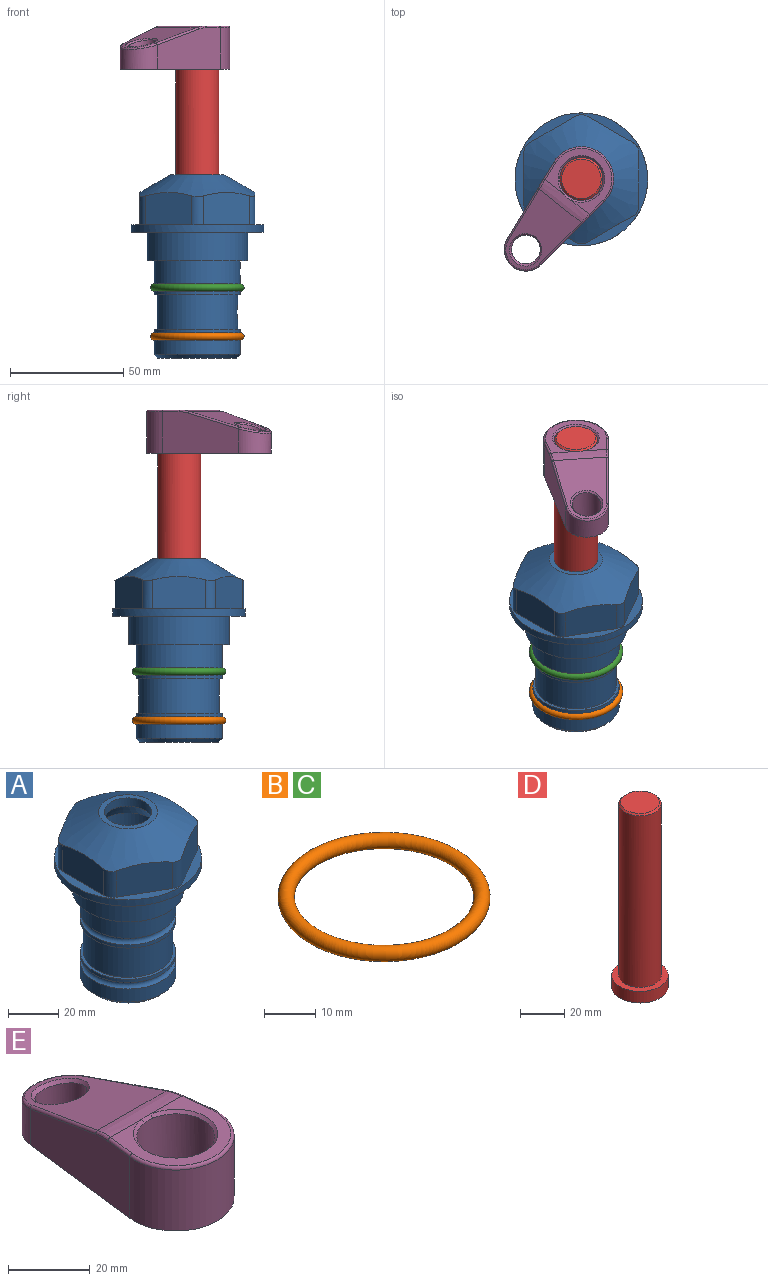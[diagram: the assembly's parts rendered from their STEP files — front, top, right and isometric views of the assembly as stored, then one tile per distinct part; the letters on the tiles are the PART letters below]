
ASSEMBLY  parts=5 mates=3
PART A: 36 faces, bbox 58.7x58.7x81 mm
  f0: cylinder r=17.78mm len=35.56mm, axis (0,0,1), area 1670.8mm2, adj f23,f24,f31
  f1: cylinder r=19.05mm len=38.1mm, axis (0,0,1), area 1191.9mm2, adj f26,f27,f30
  f2: plane 58.66x58.66mm, normal (0,0,-1), area 1150.6mm2, adj f3,f28
  f3: cylinder r=29.33mm len=58.66mm, axis (0,0,-1), area 585.1mm2, adj f2,f4
  f4: plane 58.66x58.66mm, normal (0,0,1), area 475.9mm2, adj f3,f5,f6,f7,f8,f9,f10,f11
  f5: plane 20.32x14.34mm, normal (-0.5,0.87,0), area 324.4mm2, adj f4,f15,f16,f17
  f6: plane 20.32x14.34mm, normal (0.5,0.87,0), area 324.4mm2, adj f4,f14,f15,f17
  f7: plane 23.48x14.34mm, normal (1,0,0), area 324.4mm2, adj f4,f13,f14,f17
  f8: plane 20.32x14.34mm, normal (0.5,-0.87,0), area 324.4mm2, adj f4,f12,f13,f17
  f9: plane 20.32x14.34mm, normal (-0.5,-0.87,0), area 324.4mm2, adj f4,f11,f12,f17
  f10: plane 23.48x14.34mm, normal (-1,0,0), area 324.4mm2, adj f4,f11,f16,f17
  f11: cylinder r=5.08mm len=12.85mm, axis (0,0,-1), area 67.2mm2, adj f4,f9,f10,f17
  f12: cylinder r=5.08mm len=12.85mm, axis (0,0,-1), area 67.2mm2, adj f4,f8,f9,f17
  f13: cylinder r=5.08mm len=12.85mm, axis (0,0,-1), area 67.2mm2, adj f4,f7,f8,f17
  f14: cylinder r=5.08mm len=12.85mm, axis (0,0,-1), area 67.2mm2, adj f4,f6,f7,f17
  f15: cylinder r=5.08mm len=12.85mm, axis (0,0,-1), area 67.2mm2, adj f4,f5,f6,f17
  f16: cylinder r=5.08mm len=12.85mm, axis (0,0,-1), area 67.2mm2, adj f4,f5,f10,f17
  f17: cone r=11.73mm half-angle=60deg, axis (0,0,-1), area 2071.8mm2, adj f5,f6,f7,f8,f9,f10,f11,f12
  f18: plane 23.46x23.46mm, normal (0,0,1), area 147.4mm2, adj f17,f35
  f19: plane 34.93x34.93mm, normal (0,0,-1), area 958mm2, adj f29
  f20: cylinder r=19.05mm len=38.1mm, axis (0,0,1), area 760.1mm2, adj f21,f29
  f21: torus R=19.05mm, axis (0,0,1), area 565.3mm2, adj f20,f22
  f22: cylinder r=19.05mm len=38.1mm, axis (0,0,1), area 190mm2, adj f21,f23
  f23: plane 38.1x38.1mm, normal (0,0,1), area 146.9mm2, adj f0,f22
  f24: plane 38.1x38.1mm, normal (0,0,-1), area 146.9mm2, adj f0,f25
  f25: cylinder r=19.05mm len=38.1mm, axis (0,0,1), area 190mm2, adj f24,f26
  f26: torus R=19.05mm, axis (0,0,1), area 565.3mm2, adj f1,f25
  f27: plane 44.45x44.45mm, normal (0,0,-1), area 411.7mm2, adj f1,f28
  f28: cylinder r=22.23mm len=44.45mm, axis (0,0,1), area 1773.5mm2, adj f2,f27
  f29: cone r=19.05mm half-angle=45deg, axis (0,0,1), area 257.5mm2, adj f19,f20
  f30: cylinder r=3.17mm len=6.75mm, axis (-1,0,0), area 128mm2, adj f1,f33
  f31: cylinder r=3.17mm len=6.35mm, axis (-1,0,0), area 102.5mm2, adj f0,f33
  f32: plane 25.4x25.4mm, normal (0,0,1), area 506.7mm2, adj f33
  f33: cylinder r=12.7mm len=66.42mm, axis (0,0,-1), area 5236.2mm2, adj f30,f31,f32,f34
  f34: cone r=9.53mm half-angle=30deg, axis (0,0,-1), area 443.4mm2, adj f33,f35
  f35: cylinder r=9.53mm len=19.05mm, axis (0,0,-1), area 240.9mm2, adj f18,f34
PART B: 1 faces, bbox 44.7x44.7x3.2 mm
  f0: torus R=19.05mm, axis (0,0,1), area 1193.9mm2
PART C: same geometry as B
PART D: 6 faces, bbox 25.4x25.4x101.6 mm
  f0: plane 17.46x17.46mm, normal (0,0,1), area 239.5mm2, adj f5
  f1: plane 25.4x25.4mm, normal (0,0,-1), area 506.7mm2, adj f2
  f2: cylinder r=12.7mm len=25.4mm, axis (0,0,1), area 506.7mm2, adj f1,f3
  f3: plane 25.4x25.4mm, normal (0,0,1), area 221.7mm2, adj f2,f4
  f4: cylinder r=9.53mm len=94.46mm, axis (0,0,1), area 5653mm2, adj f3,f5
  f5: cone r=8.73mm half-angle=45deg, axis (0,0,-1), area 64.4mm2, adj f0,f4
PART E: 31 faces, bbox 31.7x65.5x19.8 mm
  f0: plane 39.12x18.26mm, normal (0.99,0.12,0), area 612.2mm2, adj f1,f4,f7,f11,f13,f15
  f1: cylinder r=9.53mm len=18.91mm, axis (0,0,-1), area 296.1mm2, adj f0,f2,f7,f17
  f2: plane 39.12x18.26mm, normal (-0.99,0.12,0), area 612.2mm2, adj f1,f4,f7,f12,f14,f16
  f3: cylinder r=6.35mm len=12.7mm, axis (0,0,-1), area 362.4mm2, adj f7,f18
  f4: cylinder r=14.29mm len=28.58mm, axis (0,0,-1), area 882.2mm2, adj f0,f2,f7,f10
  f5: cylinder r=9.53mm len=19.05mm, axis (0,0,-1), area 1092.6mm2, adj f7,f19,f20
  f6: plane 26.99x23.69mm, normal (0,0,1), area 216.2mm2, adj f9,f10,f11,f12,f19
  f7: plane 63.5x28.58mm, normal (0,0,-1), area 661.8mm2, adj f0,f1,f2,f3,f4,f5,f22,f23
  f8: plane 33.52x23.6mm, normal (0,0.26,0.97), area 486mm2, adj f9,f15,f16,f17,f18
  f9: cylinder r=19.05mm len=24.72mm, axis (1,0,0), area 120.4mm2, adj f6,f8,f13,f14,f20
  f10: torus R=13.49mm, axis (0,0,1), area 59mm2, adj f4,f6,f11,f12
  f11: cylinder r=0.79mm len=8.67mm, axis (0.12,-0.99,0), area 10.8mm2, adj f0,f6,f10,f13
  f12: cylinder r=0.79mm len=8.67mm, axis (0.12,0.99,0), area 10.8mm2, adj f2,f6,f10,f14
  f13: bspline ~4.95x1.42mm, area 6.1mm2, adj f0,f9,f11,f15
  f14: bspline ~4.95x1.42mm, area 6.1mm2, adj f2,f9,f12,f16
  f15: cylinder r=0.79mm len=25.95mm, axis (0.12,-0.96,0.26), area 32.9mm2, adj f0,f8,f13,f17
  f16: cylinder r=0.79mm len=25.95mm, axis (0.12,0.96,-0.26), area 32.9mm2, adj f2,f8,f14,f17
  f17: bspline ~18.91x8.38mm, area 30mm2, adj f1,f8,f15,f16
  f18: bspline ~14.29x14.29mm, area 48.3mm2, adj f3,f8
  f19: cone r=9.53mm half-angle=45deg, axis (0,0,1), area 66.5mm2, adj f5,f6,f20
  f20: bspline ~3.22x0.96mm, area 3.5mm2, adj f5,f9,f19
  f21: plane 2.75x2.72mm, normal (0,0,-1), area 2.9mm2, adj f23,f25,f28
  f22: plane 23.05x15.88mm, normal (-0.99,-0.12,0), area 323.6mm2, adj f7,f25,f26,f27,f28,f29
  f23: plane 23.05x15.88mm, normal (0.99,-0.12,0), area 323.6mm2, adj f7,f21,f25,f27,f28,f30
  f24: cylinder r=9.53mm len=10.69mm, axis (0,0,-1), area 114.7mm2, adj f7,f27,f29,f30
  f25: cylinder r=12.7mm len=20.59mm, axis (0,0,-1), area 381.1mm2, adj f7,f21,f22,f23,f26,f28
  f26: plane 2.75x2.72mm, normal (0,0,-1), area 2.9mm2, adj f22,f25,f28
  f27: plane 19.72x18.37mm, normal (0,-0.26,-0.97), area 291.8mm2, adj f22,f23,f24,f28,f29,f30
  f28: cylinder r=15.88mm len=19.92mm, axis (1,0,0), area 54.8mm2, adj f21,f22,f23,f25,f26,f27
  f29: cylinder r=1.59mm len=11mm, axis (0,0,-1), area 34.7mm2, adj f7,f22,f24,f27
  f30: cylinder r=1.59mm len=11mm, axis (0,0,-1), area 34.7mm2, adj f7,f23,f24,f27
PLACE A at identity fixed
PLACE B t=(0,0,-21.59)mm
PLACE C at identity
PLACE D rot(axis=(0,0,-1),128.2deg) t=(0,0,27.55)mm
PLACE E rot(axis=(0,0,1),141.8deg) t=(0,0,27.55)mm
MATE fastened B.f0 <-> A.f0  axis (0,0,1) through (0,0,-46.1)mm
MATE fastened E.f4 <-> D.f2  axis (0,0,1) through (0,0,91.05)mm
MATE cylindrical D.f2 <-> A.f0  axis (0,0,-1) through (0,0,-10.55)mm
